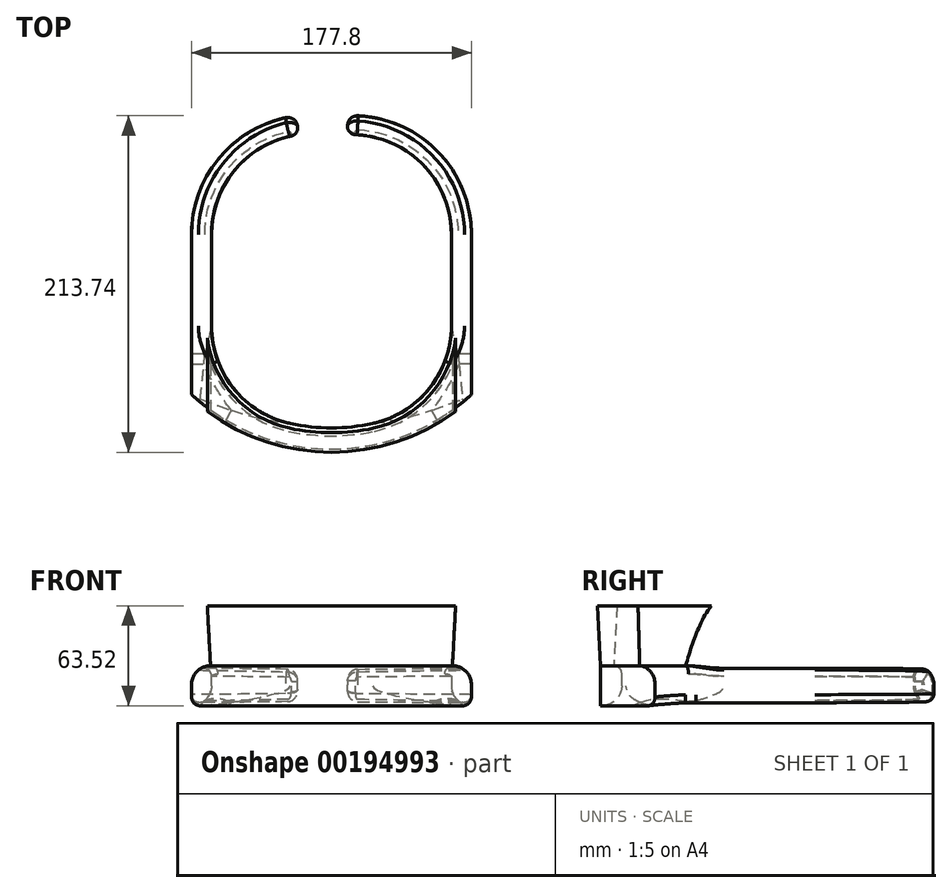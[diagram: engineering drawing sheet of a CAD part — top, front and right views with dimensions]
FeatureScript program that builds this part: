
annotation { "Feature Type Name" : "Feature", "Feature Type Description" : "" }
export const myFeature = defineFeature(function(context is Context, id is Id, definition is map)
    precondition{}
    {
        {
            var Q0;
            Q0=qCreatedBy(makeId("Top.planeOp"),FACE);
            var sketch = newSketch(context, id + "F0", { "sketchPlane" : qUnion([Q0])});
            skLineSegment(sketch, "E0", {"start": v(-46.12, 53.95) * mm, "end": v(-46.12, -42.57) * mm});
            skLineSegment(sketch, "E1", {"start": v(106.28, -42.57) * mm, "end": v(106.28, 53.95) * mm});
            skArc(sketch, "E2", {"start": v(-46.12, -42.57) * mm, "mid": v(30.08, -68.86) * mm, "end": v(106.28, -42.57) * mm});
            skLineSegment(sketch, "E3", {"start": v(-46.12, 53.95) * mm, "end": v(-58.82, 53.95) * mm});
            skLineSegment(sketch, "E4", {"start": v(-58.82, 53.95) * mm, "end": v(-58.82, -47.65) * mm});
            skLineSegment(sketch, "E5", {"start": v(106.28, 53.95) * mm, "end": v(118.98, 53.95) * mm});
            skLineSegment(sketch, "E6", {"start": v(118.98, 53.95) * mm, "end": v(118.98, -47.65) * mm});
            skArc(sketch, "E7", {"start": v(-58.82, -47.65) * mm, "mid": v(30.08, -82.35) * mm, "end": v(118.98, -47.65) * mm});
            skSolve(sketch);
        }
        {
            var Q0;
            Q0=qSketchRegion(id+"F0",true);
            extrude(context, id + "F1", {"entities" : qUnion([Q0]), "oppositeDirection" : true, "depth" : 25.4 * mm});
        }
        {
            var Q0;
            Q0=makeQuery(id+"F1.opExtrude","CAP_FACE",FACE,{"disambiguationData":[OSD([sQuery(id+"F0.wireOp",EDGE,"E0"),sQuery(id+"F0.wireOp",EDGE,"E1"),sQuery(id+"F0.wireOp",EDGE,"E2"),sQuery(id+"F0.wireOp",EDGE,"E3"),sQuery(id+"F0.wireOp",EDGE,"E4"),sQuery(id+"F0.wireOp",EDGE,"E5"),sQuery(id+"F0.wireOp",EDGE,"E6"),sQuery(id+"F0.wireOp",EDGE,"E7")])],"isStart":true});
            var sketch = newSketch(context, id + "F2", { "sketchPlane" : qUnion([Q0])});
            skArc(sketch, "E8", {"start": v(8.76, 117.38) * mm, "mid": v(-30.5, 95.9) * mm, "end": v(-46.12, 53.95) * mm});
            skArc(sketch, "E9", {"start": v(8.48, 129.4) * mm, "mid": v(-39.55, 104.5) * mm, "end": v(-58.82, 53.95) * mm});
            skLineSegment(sketch, "E10", {"start": v(8.48, 129.4) * mm, "end": v(8.76, 117.38) * mm});
            skArc(sketch, "E11", {"start": v(106.28, 53.95) * mm, "mid": v(86.84, 99.67) * mm, "end": v(40.42, 117.38) * mm});
            skArc(sketch, "E12", {"start": v(118.98, 53.95) * mm, "mid": v(95.67, 108.51) * mm, "end": v(40.13, 129.4) * mm});
            skLineSegment(sketch, "E13", {"start": v(40.42, 117.38) * mm, "end": v(40.13, 129.4) * mm});
            skSolve(sketch);
        }
        {
            var Q0;
            Q0=makeQuery(id+"F2.imprint","IMPRINT",FACE,{"disambiguationData":[TD([[makeQuery(id+"F2.imprint","IMPRINT",EDGE,{"derivedFrom":sQuery(id+"F2.wireOp",EDGE,"E8")}),-1.0]])]});
            var Q1;
            Q1=makeQuery(id+"F2.imprint","IMPRINT",FACE,{"disambiguationData":[TD([[makeQuery(id+"F2.imprint","IMPRINT",EDGE,{"derivedFrom":sQuery(id+"F2.wireOp",EDGE,"E11")}),-1.0]])]});
            extrude(context, id + "F3", {"entities" : qUnion([Q0, Q1]), "operationType" : NewBodyOperationType.ADD, "oppositeDirection" : true, "depth" : 25.4 * mm});
        }
        {
            var Q0;
            Q0=makeQuery(id+"F3.opExtrude","CAP_EDGE",EDGE,{"disambiguationData":[OSD([sQuery(id+"F2.wireOp",EDGE,"E9")])],"isStart":true});
            var Q1;
            Q1=makeQuery(id+"F1.opExtrude","CAP_EDGE",EDGE,{"disambiguationData":[OSD([sQuery(id+"F0.wireOp",EDGE,"E6")])],"isStart":true});
            fillet(context, id + "F4", {"entities" : qUnion([Q0, Q1]), "radius" : 12.06 * mm, "tangentPropagation" : true, "allowEdgeOverflow" : false});
        }
        {
            var Q0;
            Q0=makeQuery(id+"F4.opFillet","BLEND_EDGE",EDGE,{"blendedFrom":[makeQuery(id+"F3.opExtrude","CAP_EDGE",EDGE,{"disambiguationData":[OSD([sQuery(id+"F2.wireOp",EDGE,"E12")])],"isStart":true}),makeQuery(id+"F3.opExtrude","SWEPT_FACE",FACE,{"disambiguationData":[OSD([sQuery(id+"F2.wireOp",EDGE,"E13")])]})],"blendedInto":[makeQuery(id+"F3.opExtrude","SWEPT_FACE",FACE,{"disambiguationData":[OSD([sQuery(id+"F2.wireOp",EDGE,"E13")])]})]});
            var Q1;
            Q1=makeQuery(id+"F4.opFillet","BLEND_EDGE",EDGE,{"blendedFrom":[makeQuery(id+"F3.opExtrude","CAP_EDGE",EDGE,{"disambiguationData":[OSD([sQuery(id+"F2.wireOp",EDGE,"E9")])],"isStart":true}),makeQuery(id+"F3.opExtrude","SWEPT_FACE",FACE,{"disambiguationData":[OSD([sQuery(id+"F2.wireOp",EDGE,"E10")])]})],"blendedInto":[makeQuery(id+"F3.opExtrude","SWEPT_FACE",FACE,{"disambiguationData":[OSD([sQuery(id+"F2.wireOp",EDGE,"E10")])]})]});
            fillet(context, id + "F5", {"entities" : qUnion([Q0, Q1]), "radius" : 6.35 * mm, "tangentPropagation" : true, "allowEdgeOverflow" : false});
        }
        {
            var Q0;
            Q0=makeQuery(id+"F3.opExtrude","CAP_EDGE",EDGE,{"disambiguationData":[OSD([sQuery(id+"F2.wireOp",EDGE,"E8")])],"isStart":false});
            var Q1;
            Q1=makeQuery(id+"F3.opExtrude","CAP_EDGE",EDGE,{"disambiguationData":[OSD([sQuery(id+"F2.wireOp",EDGE,"E11")])],"isStart":false});
            fillet(context, id + "F6", {"entities" : qUnion([Q0, Q1]), "radius" : 12.7 * mm, "tangentPropagation" : true, "allowEdgeOverflow" : false});
        }
        {
            var Q0;
            Q0=makeQuery(id+"F1.opExtrude","CAP_EDGE",EDGE,{"disambiguationData":[OSD([sQuery(id+"F0.wireOp",EDGE,"E2")])],"isStart":false});
            fillet(context, id + "F7", {"entities" : qUnion([Q0]), "radius" : 12.7 * mm, "tangentPropagation" : true, "allowEdgeOverflow" : false});
        }
        {
            var Q0;
            Q0=makeQuery(id+"F1.opExtrude","SWEPT_EDGE",EDGE,{"disambiguationData":[OSD([sQuery(id+"F0.wireOp",EDGE,"E1"),sQuery(id+"F0.wireOp",EDGE,"E2")])]});
            var Q1;
            Q1=makeQuery(id+"F1.opExtrude","SWEPT_EDGE",EDGE,{"disambiguationData":[OSD([sQuery(id+"F0.wireOp",EDGE,"E0"),sQuery(id+"F0.wireOp",EDGE,"E2")])]});
            fillet(context, id + "F8", {"entities" : qUnion([Q0, Q1]), "radius" : 63.5 * mm, "tangentPropagation" : true, "allowEdgeOverflow" : false});
        }
        {
            var Q0;
            Q0=makeQuery(id+"F6.opFillet","BLEND_EDGE",EDGE,{"blendedFrom":[makeQuery(id+"F3.opExtrude","CAP_EDGE",EDGE,{"disambiguationData":[OSD([sQuery(id+"F2.wireOp",EDGE,"E8")])],"isStart":false}),makeQuery(id+"F3.opExtrude","SWEPT_FACE",FACE,{"disambiguationData":[OSD([sQuery(id+"F2.wireOp",EDGE,"E9")])]})],"blendedInto":[makeQuery(id+"F3.opExtrude","SWEPT_FACE",FACE,{"disambiguationData":[OSD([sQuery(id+"F2.wireOp",EDGE,"E9")])]})]});
            var Q1;
            Q1=makeQuery(id+"F6.opFillet","BLEND_EDGE",EDGE,{"blendedFrom":[makeQuery(id+"F3.opExtrude","CAP_EDGE",EDGE,{"disambiguationData":[OSD([sQuery(id+"F2.wireOp",EDGE,"E11")])],"isStart":false}),makeQuery(id+"F3.opExtrude","SWEPT_FACE",FACE,{"disambiguationData":[OSD([sQuery(id+"F2.wireOp",EDGE,"E12")])]})],"blendedInto":[makeQuery(id+"F3.opExtrude","SWEPT_FACE",FACE,{"disambiguationData":[OSD([sQuery(id+"F2.wireOp",EDGE,"E12")])]})]});
            fillet(context, id + "F9", {"entities" : qUnion([Q0, Q1]), "radius" : 5.08 * mm, "tangentPropagation" : true, "allowEdgeOverflow" : false});
        }
        {
            var Q0;
            {var subQ0=sQuery(id+"F0.wireOp",EDGE,"E5");var subQ1=sQuery(id+"F0.wireOp",EDGE,"E3");Q0=makeQuery(id+"F3.boolean.opBoolean","MERGE",FACE,{"derivedFrom":[makeQuery(id+"F1.opExtrude","CAP_FACE",FACE,{"disambiguationData":[OSD([sQuery(id+"F0.wireOp",EDGE,"E0"),sQuery(id+"F0.wireOp",EDGE,"E1"),sQuery(id+"F0.wireOp",EDGE,"E2"),subQ1,sQuery(id+"F0.wireOp",EDGE,"E4"),subQ0,sQuery(id+"F0.wireOp",EDGE,"E6"),sQuery(id+"F0.wireOp",EDGE,"E7")])],"isStart":true}),makeQuery(id+"F3.opExtrude","CAP_FACE",FACE,{"disambiguationData":[OSD([subQ1,sQuery(id+"F2.wireOp",EDGE,"E8"),sQuery(id+"F2.wireOp",EDGE,"E9"),sQuery(id+"F2.wireOp",EDGE,"E10")])],"isStart":true}),makeQuery(id+"F3.opExtrude","CAP_FACE",FACE,{"disambiguationData":[OSD([subQ0,sQuery(id+"F2.wireOp",EDGE,"E11"),sQuery(id+"F2.wireOp",EDGE,"E12"),sQuery(id+"F2.wireOp",EDGE,"E13")])],"isStart":true})]});}
            extrude(context, id + "F10", {"entities" : qUnion([Q0]), "operationType" : NewBodyOperationType.ADD, "depth" : 38.1 * mm, "hasDraft" : true, "draftAngle" : 3 * degree});
        }
    });
